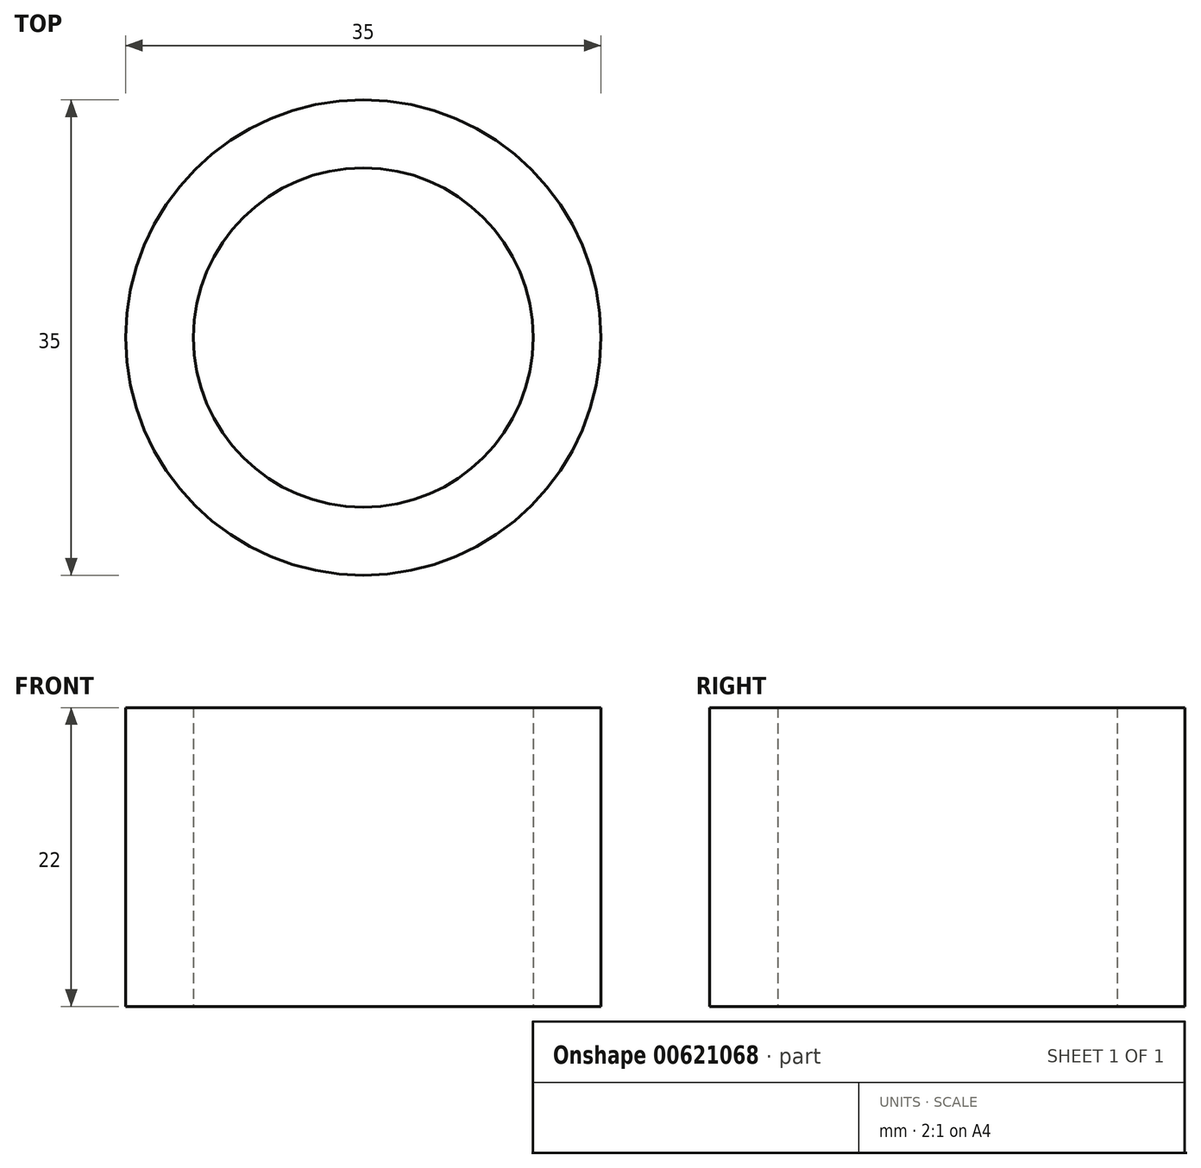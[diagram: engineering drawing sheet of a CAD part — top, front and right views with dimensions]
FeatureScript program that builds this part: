
annotation { "Feature Type Name" : "Feature", "Feature Type Description" : "" }
export const myFeature = defineFeature(function(context is Context, id is Id, definition is map)
    precondition{}
    {
        {
            var Q0;
            Q0=qCreatedBy(makeId("Top.planeOp"),FACE);
            var sketch = newSketch(context, id + "F0", { "sketchPlane" : qUnion([Q0])});
            skCircle(sketch, "E0", {"center": v(0, 0) * mm, "radius": 17.5 * mm});
            skCircle(sketch, "E1", {"center": v(0, 0) * mm, "radius": 12.5 * mm});
            skSolve(sketch);
        }
        {
            var Q0;
            Q0=makeQuery(id+"F0.imprint","IMPRINT",FACE,{"disambiguationData":[TD([[makeQuery(id+"F0.imprint","IMPRINT",EDGE,{"derivedFrom":sQuery(id+"F0.wireOp",EDGE,"E0")}),1.0]])]});
            extrude(context, id + "F1", {"entities" : qUnion([Q0]), "depth" : 22 * mm, "offsetDistance" : 25 * mm});
        }
    });
